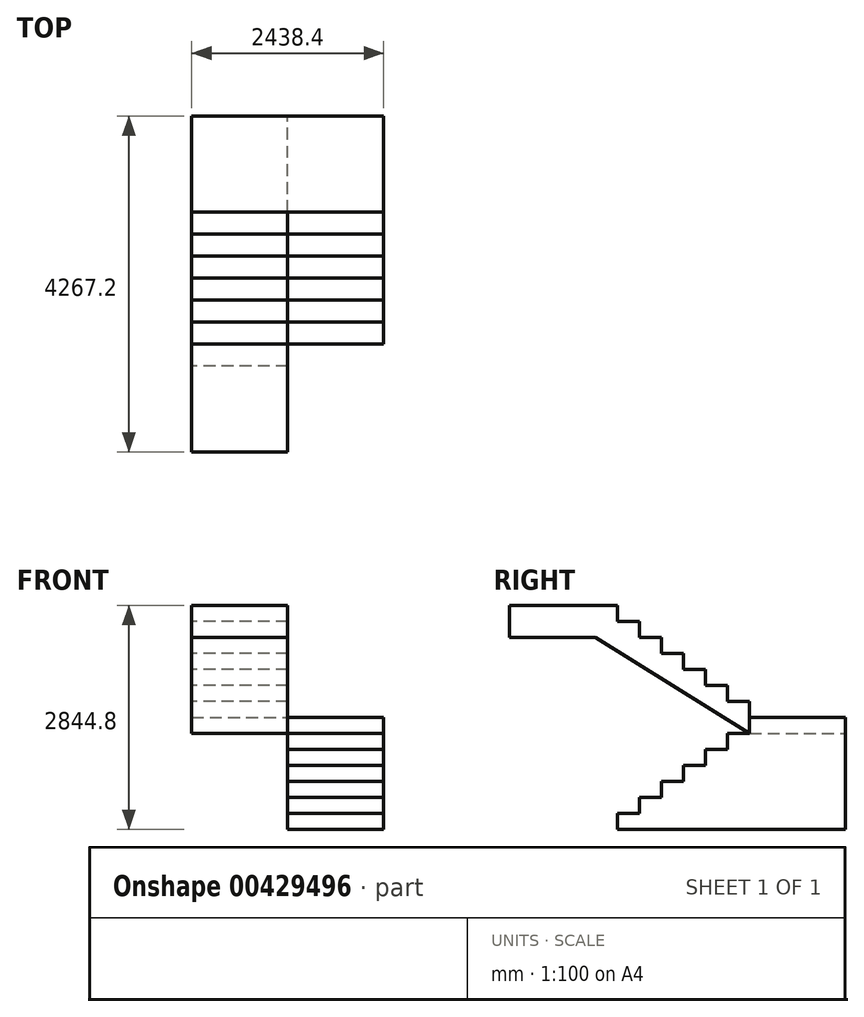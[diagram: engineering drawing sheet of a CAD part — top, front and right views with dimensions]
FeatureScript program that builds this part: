
annotation { "Feature Type Name" : "Feature", "Feature Type Description" : "" }
export const myFeature = defineFeature(function(context is Context, id is Id, definition is map)
    precondition{}
    {
        {
            var Q0;
            Q0=qCreatedBy(makeId("Right.planeOp"),FACE);
            var sketch = newSketch(context, id + "F0", { "sketchPlane" : qUnion([Q0])});
            skLineSegment(sketch, "E0", {"start": v(0, 0) * mm, "end": v(0, 203.2) * mm});
            skLineSegment(sketch, "E1", {"start": v(0, 203.2) * mm, "end": v(279.4, 203.2) * mm});
            skLineSegment(sketch, "E2", {"start": v(279.4, 203.2) * mm, "end": v(279.4, 406.4) * mm});
            skLineSegment(sketch, "E3", {"start": v(279.4, 406.4) * mm, "end": v(558.8, 406.4) * mm});
            skLineSegment(sketch, "E4", {"start": v(558.8, 406.4) * mm, "end": v(558.8, 609.6) * mm});
            skLineSegment(sketch, "E5", {"start": v(558.8, 609.6) * mm, "end": v(838.2, 609.6) * mm});
            skLineSegment(sketch, "E6", {"start": v(838.2, 609.6) * mm, "end": v(838.2, 812.8) * mm});
            skLineSegment(sketch, "E7", {"start": v(838.2, 812.8) * mm, "end": v(1117.6, 812.8) * mm});
            skLineSegment(sketch, "E8", {"start": v(1117.6, 812.8) * mm, "end": v(1117.6, 1016) * mm});
            skLineSegment(sketch, "E9", {"start": v(1117.6, 1016) * mm, "end": v(1397, 1016) * mm});
            skLineSegment(sketch, "E10", {"start": v(1397, 1016) * mm, "end": v(1397, 1219.2) * mm});
            skLineSegment(sketch, "E11", {"start": v(1397, 1219.2) * mm, "end": v(1676.4, 1219.2) * mm});
            skLineSegment(sketch, "E12", {"start": v(1676.4, 1219.2) * mm, "end": v(1676.4, 1422.4) * mm});
            skLineSegment(sketch, "E13", {"start": v(1676.4, 1422.4) * mm, "end": v(2895.6, 1422.4) * mm});
            skLineSegment(sketch, "E14", {"start": v(2895.6, 1422.4) * mm, "end": v(2895.6, 0) * mm});
            skLineSegment(sketch, "E15", {"start": v(2895.6, 0) * mm, "end": v(0, 0) * mm});
            skSolve(sketch);
        }
        {
            var Q0;
            Q0 = qSketchRegion(id + "F0", true);
            extrude(context, id + "F1", {"entities" : qUnion([Q0]), "oppositeDirection" : true, "depth" : 1219.2 * mm});
        }
        {
            var Q0;
            Q0=makeQuery(id+"F1.opExtrude","CAP_FACE",FACE,{"disambiguationData":[OSD([sQuery(id+"F0.wireOp",EDGE,"E0"),sQuery(id+"F0.wireOp",EDGE,"E1"),sQuery(id+"F0.wireOp",EDGE,"E2"),sQuery(id+"F0.wireOp",EDGE,"E3"),sQuery(id+"F0.wireOp",EDGE,"E4"),sQuery(id+"F0.wireOp",EDGE,"E5"),sQuery(id+"F0.wireOp",EDGE,"E6"),sQuery(id+"F0.wireOp",EDGE,"E7"),sQuery(id+"F0.wireOp",EDGE,"E8"),sQuery(id+"F0.wireOp",EDGE,"E9"),sQuery(id+"F0.wireOp",EDGE,"E10"),sQuery(id+"F0.wireOp",EDGE,"E11"),sQuery(id+"F0.wireOp",EDGE,"E12"),sQuery(id+"F0.wireOp",EDGE,"E13"),sQuery(id+"F0.wireOp",EDGE,"E14"),sQuery(id+"F0.wireOp",EDGE,"E15")])],"isStart":false});
            var sketch = newSketch(context, id + "F2", { "sketchPlane" : qUnion([Q0])});
            skLineSegment(sketch, "E16.bottom", {"start": v(-1676.4, 1422.4) * mm, "end": v(-2895.6, 1422.4) * mm});
            skLineSegment(sketch, "E16.top", {"start": v(-1676.4, 1219.2) * mm, "end": v(-2895.6, 1219.2) * mm});
            skLineSegment(sketch, "E16.left", {"start": v(-1676.4, 1422.4) * mm, "end": v(-1676.4, 1219.2) * mm});
            skLineSegment(sketch, "E16.right", {"start": v(-2895.6, 1422.4) * mm, "end": v(-2895.6, 1219.2) * mm});
            skSolve(sketch);
        }
        {
            var Q0;
            Q0 = qSketchRegion(id + "F2", true);
            extrude(context, id + "F3", {"entities" : qUnion([Q0]), "operationType" : NewBodyOperationType.ADD, "depth" : 1219.2 * mm});
        }
        {
            var Q0;
            Q0=makeQuery(id+"F3.opExtrude","CAP_FACE",FACE,{"disambiguationData":[OSD([sQuery(id+"F2.wireOp",EDGE,"E16.bottom"),sQuery(id+"F2.wireOp",EDGE,"E16.top"),sQuery(id+"F2.wireOp",EDGE,"E16.left"),sQuery(id+"F2.wireOp",EDGE,"E16.right")])],"isStart":false});
            var sketch = newSketch(context, id + "F4", { "sketchPlane" : qUnion([Q0])});
            skLineSegment(sketch, "E17", {"start": v(-1676.4, 1219.2) * mm, "end": v(-1676.4, 1625.6) * mm});
            skLineSegment(sketch, "E18", {"start": v(-1676.4, 1625.6) * mm, "end": v(-1397, 1625.6) * mm});
            skLineSegment(sketch, "E19", {"start": v(-1397, 1625.6) * mm, "end": v(-1397, 1828.8) * mm});
            skLineSegment(sketch, "E20", {"start": v(-1397, 1828.8) * mm, "end": v(-1117.6, 1828.8) * mm});
            skLineSegment(sketch, "E21", {"start": v(-1117.6, 1828.8) * mm, "end": v(-1117.6, 2032) * mm});
            skLineSegment(sketch, "E22", {"start": v(-1117.6, 2032) * mm, "end": v(-838.2, 2032) * mm});
            skLineSegment(sketch, "E23", {"start": v(-838.2, 2032) * mm, "end": v(-838.2, 2235.2) * mm});
            skLineSegment(sketch, "E24", {"start": v(-838.2, 2235.2) * mm, "end": v(-558.8, 2235.2) * mm});
            skLineSegment(sketch, "E25", {"start": v(-558.8, 2235.2) * mm, "end": v(-558.8, 2438.4) * mm});
            skLineSegment(sketch, "E26", {"start": v(-558.8, 2438.4) * mm, "end": v(-279.4, 2438.4) * mm});
            skLineSegment(sketch, "E27", {"start": v(-279.4, 2438.4) * mm, "end": v(-279.4, 2641.6) * mm});
            skLineSegment(sketch, "E28", {"start": v(-279.4, 2641.6) * mm, "end": v(0, 2641.6) * mm});
            skLineSegment(sketch, "E29", {"start": v(0, 2641.6) * mm, "end": v(0, 2844.8) * mm});
            skLineSegment(sketch, "E30", {"start": v(0, 2844.8) * mm, "end": v(279.4, 2844.8) * mm});
            skLineSegment(sketch, "E31", {"start": v(279.4, 2844.8) * mm, "end": v(279.4, 2438.4) * mm});
            skLineSegment(sketch, "E32", {"start": v(279.4, 2438.4) * mm, "end": v(-1676.4, 1219.2) * mm});
            skSolve(sketch);
        }
        {
            var Q0;
            Q0 = qSketchRegion(id + "F4", true);
            var Q1;
            Q1=makeQuery(id+"F1.opExtrude","CAP_FACE",FACE,{"disambiguationData":[OSD([sQuery(id+"F0.wireOp",EDGE,"E0"),sQuery(id+"F0.wireOp",EDGE,"E1"),sQuery(id+"F0.wireOp",EDGE,"E2"),sQuery(id+"F0.wireOp",EDGE,"E3"),sQuery(id+"F0.wireOp",EDGE,"E4"),sQuery(id+"F0.wireOp",EDGE,"E5"),sQuery(id+"F0.wireOp",EDGE,"E6"),sQuery(id+"F0.wireOp",EDGE,"E7"),sQuery(id+"F0.wireOp",EDGE,"E8"),sQuery(id+"F0.wireOp",EDGE,"E9"),sQuery(id+"F0.wireOp",EDGE,"E10"),sQuery(id+"F0.wireOp",EDGE,"E11"),sQuery(id+"F0.wireOp",EDGE,"E12"),sQuery(id+"F0.wireOp",EDGE,"E13"),sQuery(id+"F0.wireOp",EDGE,"E14"),sQuery(id+"F0.wireOp",EDGE,"E15")])],"isStart":false});
            extrude(context, id + "F5", {"entities" : qUnion([Q0]), "operationType" : NewBodyOperationType.ADD, "endBound" : BoundingType.UP_TO_SURFACE, "oppositeDirection" : true, "endBoundEntityFace" : qUnion([Q1]), "depth" : 25.4 * mm});
        }
        {
            var Q0;
            Q0=makeQuery(id+"F5.opExtrude","SWEPT_FACE",FACE,{"disambiguationData":[OSD([sQuery(id+"F4.wireOp",EDGE,"E31")])]});
            var sketch = newSketch(context, id + "F6", { "sketchPlane" : qUnion([Q0])});
            skLineSegment(sketch, "E33.0", {"start": v(-1219.2, 2844.8) * mm, "end": v(-2438.4, 2844.8) * mm});
            skLineSegment(sketch, "E33.1", {"start": v(-2438.4, 2844.8) * mm, "end": v(-2438.4, 2438.4) * mm});
            skLineSegment(sketch, "E33.2", {"start": v(-1219.2, 2438.4) * mm, "end": v(-2438.4, 2438.4) * mm});
            skLineSegment(sketch, "E33.3", {"start": v(-1219.2, 2844.8) * mm, "end": v(-1219.2, 2438.4) * mm});
            skSolve(sketch);
        }
        {
            var Q0;
            Q0 = qSketchRegion(id + "F6", true);
            extrude(context, id + "F7", {"entities" : qUnion([Q0]), "operationType" : NewBodyOperationType.ADD, "depth" : 1092.2 * mm});
        }
    });
